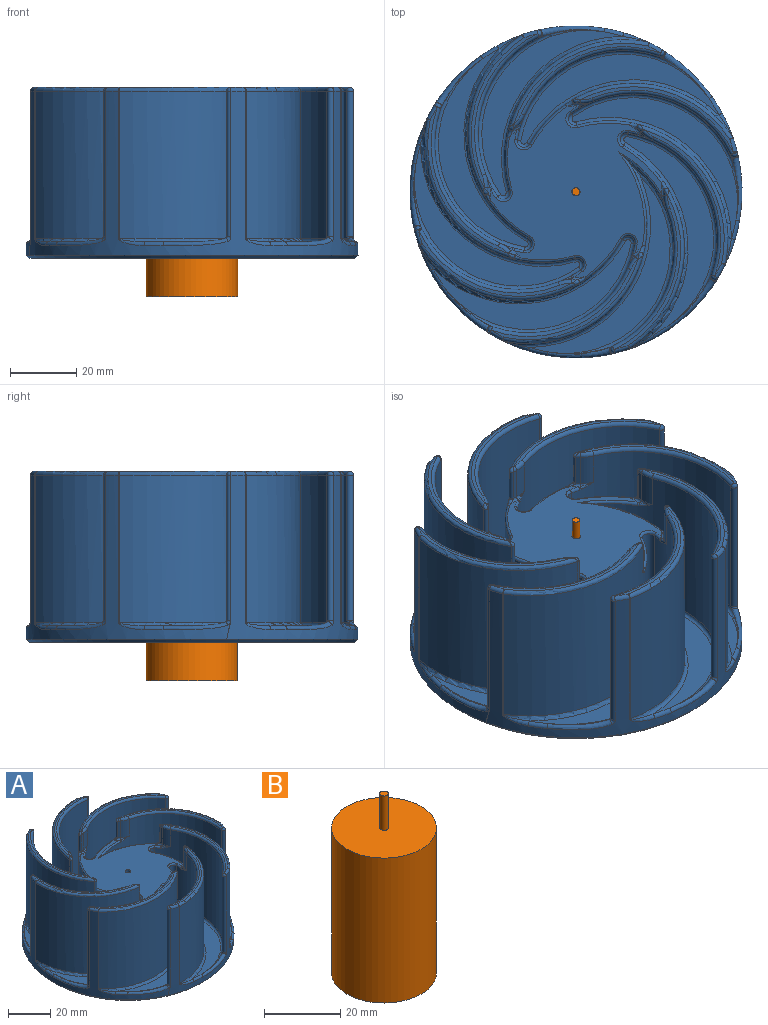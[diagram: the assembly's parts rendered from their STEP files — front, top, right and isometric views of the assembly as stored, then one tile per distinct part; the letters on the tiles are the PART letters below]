
ASSEMBLY  parts=2 mates=1
PART A: 279 faces, bbox 106.1x106.1x52.1 mm
  f0: bspline ~1.41x1mm, area 1.2mm2, adj f37,f60,f254,f256,f259
  f1: bspline ~1.5x1.09mm, area 1.2mm2, adj f31,f61,f234,f236,f239
  f2: bspline ~1.41x1mm, area 1.2mm2, adj f42,f62,f216,f218,f221
  f3: bspline ~1.5x1.09mm, area 1.2mm2, adj f39,f63,f196,f198,f201
  f4: bspline ~1.41x1mm, area 1.2mm2, adj f45,f64,f210,f211,f214
  f5: bspline ~1.5x1.09mm, area 1.2mm2, adj f44,f65,f231,f232,f235
  f6: bspline ~1.41x1mm, area 1.2mm2, adj f36,f66,f251,f252,f255
  f7: bspline ~1.5x1.09mm, area 1.2mm2, adj f33,f67,f269,f271,f272
  f8: bspline ~2.35x1.6mm, area 2.9mm2, adj f16,f32,f48,f153,f157
  f9: bspline ~2.3x1.86mm, area 2.9mm2, adj f17,f41,f48,f125,f126
  f10: bspline ~2.35x1.6mm, area 2.9mm2, adj f18,f40,f48,f97,f98
  f11: bspline ~2.3x1.86mm, area 2.9mm2, adj f19,f46,f48,f95,f99
  f12: bspline ~2.35x1.6mm, area 2.9mm2, adj f20,f43,f48,f123,f127
  f13: bspline ~2.3x1.86mm, area 2.9mm2, adj f21,f35,f48,f151,f154
  f14: bspline ~2.35x1.6mm, area 2.9mm2, adj f22,f34,f48,f178,f182
  f15: bspline ~2.3x1.86mm, area 2.9mm2, adj f23,f38,f48,f180,f181
  f16: bspline ~18.89x13.53mm, area 40.2mm2, adj f8,f48,f157,f161
  f17: bspline ~21.98x6.12mm, area 40.2mm2, adj f9,f48,f125,f134
  f18: bspline ~18.89x13.53mm, area 40.2mm2, adj f10,f48,f97,f106
  f19: bspline ~21.98x6.12mm, area 40.2mm2, adj f11,f48,f94,f95
  f20: bspline ~18.89x13.53mm, area 40.2mm2, adj f12,f48,f122,f123
  f21: bspline ~21.98x6.12mm, area 40.2mm2, adj f13,f48,f150,f151
  f22: bspline ~18.89x13.53mm, area 40.2mm2, adj f14,f48,f177,f178
  f23: bspline ~21.98x6.12mm, area 40.2mm2, adj f15,f48,f180,f189
  f24: plane 39.79x30.16mm, normal (0,0,1), area 51.4mm2, adj f183,f184,f187,f190,f191
  f25: plane 48.44x15.03mm, normal (0,0,1), area 51.4mm2, adj f166,f167,f171,f175,f176
  f26: plane 39.79x30.16mm, normal (0,0,1), area 51.4mm2, adj f139,f140,f144,f148,f149
  f27: plane 48.44x15.03mm, normal (0,0,1), area 51.4mm2, adj f111,f112,f116,f120,f121
  f28: plane 39.79x30.16mm, normal (0,0,1), area 51.4mm2, adj f84,f85,f88,f92,f93
  f29: plane 48.44x15.03mm, normal (0,0,1), area 51.4mm2, adj f100,f101,f104,f107,f108
  f30: plane 39.79x30.16mm, normal (0,0,1), area 51.4mm2, adj f128,f129,f132,f135,f136
  f31: cylinder r=35.7mm len=61.85mm, axis (0,0,1), area 3395.5mm2, adj f1,f32,f160,f167,f168,f233,f234,f236
  f32: cylinder r=32.5mm len=44.3mm, axis (0,0,1), area 2790.1mm2, adj f8,f31,f71,f148,f153,f157,f222,f225
  f33: cylinder r=35.7mm len=59.91mm, axis (0,0,1), area 3043.9mm2, adj f7,f78,f163,f169,f170,f270,f271,f272
  f34: cylinder r=32.5mm len=44.3mm, axis (0,0,1), area 2416.6mm2, adj f14,f69,f78,f178,f182,f183,f260,f262
  f35: cylinder r=32.5mm len=49.43mm, axis (0,0,1), area 2416.6mm2, adj f13,f76,f79,f151,f154,f155,f263,f264
  f36: cylinder r=35.7mm len=51.3mm, axis (0,0,1), area 3043.9mm2, adj f6,f79,f136,f142,f143,f251,f255,f258
  f37: cylinder r=35.7mm len=51.3mm, axis (0,0,1), area 3043.9mm2, adj f0,f77,f188,f191,f194,f253,f254,f256
  f38: cylinder r=32.5mm len=49.43mm, axis (0,0,1), area 2416.6mm2, adj f15,f70,f77,f175,f180,f181,f240,f242
  f39: cylinder r=35.7mm len=59.91mm, axis (0,0,1), area 3043.9mm2, adj f3,f82,f105,f112,f113,f196,f197,f198
  f40: cylinder r=32.5mm len=44.3mm, axis (0,0,1), area 2416.6mm2, adj f10,f73,f82,f92,f97,f98,f203,f204
  f41: cylinder r=32.5mm len=49.43mm, axis (0,0,1), area 2416.6mm2, adj f9,f72,f83,f120,f125,f126,f202,f205
  f42: cylinder r=35.7mm len=51.3mm, axis (0,0,1), area 3043.9mm2, adj f2,f83,f133,f140,f141,f215,f216,f218
  f43: cylinder r=32.5mm len=44.3mm, axis (0,0,1), area 2416.6mm2, adj f12,f75,f80,f123,f127,f128,f243,f244
  f44: cylinder r=35.7mm len=59.91mm, axis (0,0,1), area 3043.9mm2, adj f5,f80,f108,f114,f115,f231,f235,f238
  f45: cylinder r=35.7mm len=51.3mm, axis (0,0,1), area 3043.9mm2, adj f4,f81,f85,f86,f87,f210,f214,f217
  f46: cylinder r=32.5mm len=49.43mm, axis (0,0,1), area 2416.6mm2, adj f11,f74,f81,f95,f99,f100,f223,f224
  f47: plane 48.44x15.03mm, normal (0,0,1), area 51.4mm2, adj f155,f156,f159,f162,f163
  f48: cylinder r=50mm len=100mm, axis (0,0,-1), area 2743.9mm2, adj f8,f9,f10,f11,f12,f13,f14,f15
  f49: plane 98x98mm, normal (0,0,-1), area 6738.7mm2, adj f275,f276
  f50: cylinder r=15mm len=33mm, axis (0,0,-1), area 3110.2mm2, adj f275,f278
  f51: plane 28x28mm, normal (0,0,-1), area 599.8mm2, adj f277,f278
  f52: plane 57.4x36.6mm, normal (0,0,1), area 406mm2, adj f157,f160,f161
  f53: plane 57.4x32.34mm, normal (0,0,1), area 402.5mm2, adj f170,f174,f177,f178
  f54: plane 53.9x37.11mm, normal (0,0,1), area 402.5mm2, adj f143,f147,f150,f151
  f55: plane 53.9x37.11mm, normal (0,0,1), area 402.5mm2, adj f180,f185,f188,f189
  f56: plane 57.4x32.34mm, normal (0,0,1), area 402.5mm2, adj f97,f102,f105,f106
  f57: plane 53.9x37.11mm, normal (0,0,1), area 402.5mm2, adj f125,f130,f133,f134
  f58: plane 57.4x32.34mm, normal (0,0,1), area 402.5mm2, adj f115,f119,f122,f123
  f59: plane 53.9x37.11mm, normal (0,0,1), area 402.5mm2, adj f87,f91,f94,f95
  f60: cylinder r=26.54mm len=9.65mm, axis (0,0,1), area 12.9mm2, adj f0,f69,f187,f254,f259
  f61: cylinder r=26.54mm len=9.65mm, axis (0,0,1), area 12.9mm2, adj f1,f70,f166,f234,f239
  f62: cylinder r=26.54mm len=9.65mm, axis (0,0,1), area 12.9mm2, adj f2,f71,f139,f216,f221
  f63: cylinder r=26.54mm len=9.65mm, axis (0,0,1), area 12.9mm2, adj f3,f72,f111,f196,f201
  f64: cylinder r=26.54mm len=9.65mm, axis (0,0,1), area 12.9mm2, adj f4,f73,f84,f210,f211
  f65: cylinder r=26.54mm len=9.65mm, axis (0,0,1), area 12.9mm2, adj f5,f74,f104,f231,f232
  f66: cylinder r=26.54mm len=9.65mm, axis (0,0,1), area 12.9mm2, adj f6,f75,f132,f251,f252
  f67: cylinder r=26.54mm len=9.65mm, axis (0,0,1), area 12.9mm2, adj f7,f76,f159,f269,f272
  f68: plane 51.02x51.02mm, normal (0,0,1), area 1459.3mm2, adj f197,f200,f201,f204,f209,f211,f212,f215
  f69: cylinder r=10mm len=9.65mm, axis (0,0,1), area 40.6mm2, adj f34,f60,f184,f257
  f70: cylinder r=10mm len=9.65mm, axis (0,0,1), area 40.6mm2, adj f38,f61,f171,f237
  f71: cylinder r=10mm len=9.65mm, axis (0,0,1), area 40.6mm2, adj f32,f62,f144,f219
  f72: cylinder r=10mm len=9.65mm, axis (0,0,1), area 40.6mm2, adj f41,f63,f116,f199
  f73: cylinder r=10mm len=9.65mm, axis (0,0,1), area 40.6mm2, adj f40,f64,f88,f207
  f74: cylinder r=10mm len=9.65mm, axis (0,0,1), area 40.6mm2, adj f46,f65,f101,f227
  f75: cylinder r=10mm len=9.65mm, axis (0,0,1), area 40.6mm2, adj f43,f66,f129,f247
  f76: cylinder r=10mm len=9.65mm, axis (0,0,1), area 40.6mm2, adj f35,f67,f156,f266
  f77: cylinder r=2mm len=33.15mm, axis (0,0,1), area 186.1mm2, adj f37,f38,f185,f249
  f78: cylinder r=2mm len=33.15mm, axis (0,0,1), area 186.1mm2, adj f33,f34,f174,f268
  f79: cylinder r=2mm len=33.15mm, axis (0,0,1), area 186.1mm2, adj f35,f36,f147,f261
  f80: cylinder r=2mm len=33.15mm, axis (0,0,1), area 186.1mm2, adj f43,f44,f119,f241
  f81: cylinder r=2mm len=33.15mm, axis (0,0,1), area 186.1mm2, adj f45,f46,f91,f220
  f82: cylinder r=2mm len=33.15mm, axis (0,0,1), area 186.1mm2, adj f39,f40,f102,f200
  f83: cylinder r=2mm len=33.15mm, axis (0,0,1), area 186.1mm2, adj f41,f42,f130,f212
  f84: torus R=27.64mm, axis (0,0,1), area 1.5mm2, adj f28,f64,f88,f206
  f85: torus R=34.6mm, axis (0,0,1), area 91.4mm2, adj f28,f45,f89,f206
  f86: cylinder r=1.1mm len=44.3mm, axis (0,0,1), area 12mm2, adj f45,f48,f89,f90
  f87: torus R=36.8mm, axis (0,0,1), area 121.6mm2, adj f45,f59,f90,f91
  f88: torus R=8.9mm, axis (0,0,1), area 7mm2, adj f28,f73,f84,f92
  f89: sphere r=1.1mm, area 0.3mm2, adj f85,f86,f93
  f90: bspline ~9.7x2.31mm, area 9.2mm2, adj f48,f86,f87,f94
  f91: torus R=0.9mm, axis (0,0,1), area 7.8mm2, adj f59,f81,f87,f95
  f92: torus R=33.6mm, axis (0,0,1), area 85.2mm2, adj f28,f40,f88,f96
  f93: torus R=48.9mm, axis (0,0,1), area 7.7mm2, adj f28,f48,f89,f96
  f94: torus R=48.9mm, axis (0,0,1), area 10mm2, adj f19,f48,f59,f90
  f95: torus R=31.4mm, axis (0,0,1), area 109.6mm2, adj f11,f19,f46,f59,f91
  f96: sphere r=1.1mm, area 4.4mm2, adj f92,f93,f98
  f97: torus R=31.4mm, axis (0,0,1), area 109.6mm2, adj f10,f18,f40,f56,f102
  f98: cylinder r=1.1mm len=43.79mm, axis (0,0,-1), area 141.2mm2, adj f10,f40,f48,f96
  f99: cylinder r=1.1mm len=43.79mm, axis (0,0,-1), area 141.2mm2, adj f11,f46,f48,f103
  f100: torus R=33.6mm, axis (0,0,1), area 85.2mm2, adj f29,f46,f101,f103
  f101: torus R=8.9mm, axis (0,0,1), area 7mm2, adj f29,f74,f100,f104
  f102: torus R=0.9mm, axis (0,0,1), area 7.8mm2, adj f56,f82,f97,f105
  f103: sphere r=1.1mm, area 2.9mm2, adj f99,f100,f107
  f104: torus R=27.64mm, axis (0,0,1), area 1.5mm2, adj f29,f65,f101,f226
  f105: torus R=36.8mm, axis (0,0,1), area 121.6mm2, adj f39,f56,f102,f109
  f106: torus R=48.9mm, axis (0,0,1), area 10mm2, adj f18,f48,f56,f109
  f107: torus R=48.9mm, axis (0,0,1), area 7.7mm2, adj f29,f48,f103,f110
  f108: torus R=34.6mm, axis (0,0,1), area 91.4mm2, adj f29,f44,f110,f226
  f109: bspline ~8.1x6.51mm, area 9.2mm2, adj f48,f105,f106,f113
  f110: sphere r=1.1mm, area 0.3mm2, adj f107,f108,f114
  f111: torus R=27.64mm, axis (0,0,1), area 1.5mm2, adj f27,f63,f116,f195
  f112: torus R=34.6mm, axis (0,0,1), area 91.4mm2, adj f27,f39,f117,f195
  f113: cylinder r=1.1mm len=44.3mm, axis (0,0,1), area 12mm2, adj f39,f48,f109,f117
  f114: cylinder r=1.1mm len=44.3mm, axis (0,0,1), area 12mm2, adj f44,f48,f110,f118
  f115: torus R=36.8mm, axis (0,0,1), area 121.6mm2, adj f44,f58,f118,f119
  f116: torus R=8.9mm, axis (0,0,1), area 7mm2, adj f27,f72,f111,f120
  f117: sphere r=1.1mm, area 0.3mm2, adj f112,f113,f121
  f118: bspline ~8.1x6.51mm, area 9.2mm2, adj f48,f114,f115,f122
  f119: torus R=0.9mm, axis (0,0,1), area 7.8mm2, adj f58,f80,f115,f123
  f120: torus R=33.6mm, axis (0,0,1), area 85.2mm2, adj f27,f41,f116,f124
  f121: torus R=48.9mm, axis (0,0,1), area 7.7mm2, adj f27,f48,f117,f124
  f122: torus R=48.9mm, axis (0,0,1), area 10mm2, adj f20,f48,f58,f118
  f123: torus R=31.4mm, axis (0,0,1), area 109.6mm2, adj f12,f20,f43,f58,f119
  f124: sphere r=1.1mm, area 3.5mm2, adj f120,f121,f126
  f125: torus R=31.4mm, axis (0,0,1), area 109.6mm2, adj f9,f17,f41,f57,f130
  f126: cylinder r=1.1mm len=43.79mm, axis (0,0,-1), area 141.2mm2, adj f9,f41,f48,f124
  f127: cylinder r=1.1mm len=43.79mm, axis (0,0,-1), area 141.2mm2, adj f12,f43,f48,f131
  f128: torus R=33.6mm, axis (0,0,1), area 85.2mm2, adj f30,f43,f129,f131
  f129: torus R=8.9mm, axis (0,0,1), area 7mm2, adj f30,f75,f128,f132
  f130: torus R=0.9mm, axis (0,0,1), area 7.8mm2, adj f57,f83,f125,f133
  f131: sphere r=1.1mm, area 2.9mm2, adj f127,f128,f135
  f132: torus R=27.64mm, axis (0,0,1), area 1.5mm2, adj f30,f66,f129,f246
  f133: torus R=36.8mm, axis (0,0,1), area 121.6mm2, adj f42,f57,f130,f137
  f134: torus R=48.9mm, axis (0,0,1), area 10mm2, adj f17,f48,f57,f137
  f135: torus R=48.9mm, axis (0,0,1), area 7.7mm2, adj f30,f48,f131,f138
  f136: torus R=34.6mm, axis (0,0,1), area 91.4mm2, adj f30,f36,f138,f246
  f137: bspline ~9.7x2.31mm, area 9.2mm2, adj f48,f133,f134,f141
  f138: sphere r=1.1mm, area 0.3mm2, adj f135,f136,f142
  f139: torus R=27.64mm, axis (0,0,1), area 1.5mm2, adj f26,f62,f144,f213
  f140: torus R=34.6mm, axis (0,0,1), area 91.4mm2, adj f26,f42,f145,f213
  f141: cylinder r=1.1mm len=44.3mm, axis (0,0,1), area 12mm2, adj f42,f48,f137,f145
  f142: cylinder r=1.1mm len=44.3mm, axis (0,0,1), area 12mm2, adj f36,f48,f138,f146
  f143: torus R=36.8mm, axis (0,0,1), area 121.6mm2, adj f36,f54,f146,f147
  f144: torus R=8.9mm, axis (0,0,1), area 7mm2, adj f26,f71,f139,f148
  f145: sphere r=1.1mm, area 0.3mm2, adj f140,f141,f149
  f146: bspline ~9.7x2.31mm, area 9.2mm2, adj f48,f142,f143,f150
  f147: torus R=0.9mm, axis (0,0,1), area 7.8mm2, adj f54,f79,f143,f151
  f148: torus R=33.6mm, axis (0,0,1), area 85.2mm2, adj f26,f32,f144,f152
  f149: torus R=48.9mm, axis (0,0,1), area 7.7mm2, adj f26,f48,f145,f152
  f150: torus R=48.9mm, axis (0,0,1), area 10mm2, adj f21,f48,f54,f146
  f151: torus R=31.4mm, axis (0,0,1), area 109.6mm2, adj f13,f21,f35,f54,f147
  f152: sphere r=1.1mm, area 3.5mm2, adj f148,f149,f153
  f153: cylinder r=1.1mm len=43.79mm, axis (0,0,-1), area 141.2mm2, adj f8,f32,f48,f152
  f154: cylinder r=1.1mm len=43.79mm, axis (0,0,-1), area 141.2mm2, adj f13,f35,f48,f158
  f155: torus R=33.6mm, axis (0,0,1), area 85.2mm2, adj f35,f47,f156,f158
  f156: torus R=8.9mm, axis (0,0,1), area 7mm2, adj f47,f76,f155,f159
  f157: torus R=31.4mm, axis (0,0,1), area 123.9mm2, adj f8,f16,f32,f52,f160
  f158: sphere r=1.1mm, area 3.1mm2, adj f154,f155,f162
  f159: torus R=27.64mm, axis (0,0,1), area 1.5mm2, adj f47,f67,f156,f273
  f160: torus R=36.8mm, axis (0,0,1), area 135.1mm2, adj f31,f52,f157,f164
  f161: torus R=48.9mm, axis (0,0,1), area 10mm2, adj f16,f48,f52,f164
  f162: torus R=48.9mm, axis (0,0,1), area 7.7mm2, adj f47,f48,f158,f165
  f163: torus R=34.6mm, axis (0,0,1), area 91.4mm2, adj f33,f47,f165,f273
  f164: bspline ~8.1x6.51mm, area 9.2mm2, adj f48,f160,f161,f168
  f165: sphere r=1.1mm, area 0.3mm2, adj f162,f163,f169
  f166: torus R=27.64mm, axis (0,0,1), area 1.5mm2, adj f25,f61,f171,f230
  f167: torus R=34.6mm, axis (0,0,1), area 91.4mm2, adj f25,f31,f172,f230
  f168: cylinder r=1.1mm len=44.3mm, axis (0,0,1), area 12mm2, adj f31,f48,f164,f172
  f169: cylinder r=1.1mm len=44.3mm, axis (0,0,1), area 12mm2, adj f33,f48,f165,f173
  f170: torus R=36.8mm, axis (0,0,1), area 121.6mm2, adj f33,f53,f173,f174
  f171: torus R=8.9mm, axis (0,0,1), area 7mm2, adj f25,f70,f166,f175
  f172: sphere r=1.1mm, area 0.3mm2, adj f167,f168,f176
  f173: bspline ~8.1x6.51mm, area 9.2mm2, adj f48,f169,f170,f177
  f174: torus R=0.9mm, axis (0,0,1), area 7.8mm2, adj f53,f78,f170,f178
  f175: torus R=33.6mm, axis (0,0,1), area 85.2mm2, adj f25,f38,f171,f179
  f176: torus R=48.9mm, axis (0,0,1), area 7.7mm2, adj f25,f48,f172,f179
  f177: torus R=48.9mm, axis (0,0,1), area 10mm2, adj f22,f48,f53,f173
  f178: torus R=31.4mm, axis (0,0,1), area 109.6mm2, adj f14,f22,f34,f53,f174
  f179: sphere r=1.1mm, area 2.9mm2, adj f175,f176,f181
  f180: torus R=31.4mm, axis (0,0,1), area 109.6mm2, adj f15,f23,f38,f55,f185
  f181: cylinder r=1.1mm len=43.79mm, axis (0,0,-1), area 141.2mm2, adj f15,f38,f48,f179
  f182: cylinder r=1.1mm len=43.79mm, axis (0,0,-1), area 141.2mm2, adj f14,f34,f48,f186
  f183: torus R=33.6mm, axis (0,0,1), area 85.2mm2, adj f24,f34,f184,f186
  f184: torus R=8.9mm, axis (0,0,1), area 7mm2, adj f24,f69,f183,f187
  f185: torus R=0.9mm, axis (0,0,1), area 7.8mm2, adj f55,f77,f180,f188
  f186: sphere r=1.1mm, area 3.6mm2, adj f182,f183,f190
  f187: torus R=27.64mm, axis (0,0,1), area 1.5mm2, adj f24,f60,f184,f250
  f188: torus R=36.8mm, axis (0,0,1), area 121.6mm2, adj f37,f55,f185,f192
  f189: torus R=48.9mm, axis (0,0,1), area 10mm2, adj f23,f48,f55,f192
  f190: torus R=48.9mm, axis (0,0,1), area 7.7mm2, adj f24,f48,f186,f193
  f191: torus R=34.6mm, axis (0,0,1), area 91.4mm2, adj f24,f37,f193,f250
  f192: bspline ~9.7x2.31mm, area 9.2mm2, adj f48,f188,f189,f194
  f193: sphere r=1.1mm, area 0.3mm2, adj f190,f191,f194
  f194: cylinder r=1.1mm len=44.3mm, axis (0,0,1), area 12mm2, adj f37,f48,f192,f193
  f195: bspline ~3.91x2.13mm, area 2.3mm2, adj f111,f112,f196
  f196: cylinder r=0.75mm len=9.49mm, axis (0,0,-1), area 18.7mm2, adj f3,f39,f63,f195
  f197: torus R=34.95mm, axis (0,0,1), area 19mm2, adj f39,f68,f198,f200
  f198: bspline ~2.87x2.55mm, area 3.6mm2, adj f3,f39,f197,f201
  f199: torus R=10.75mm, axis (0,0,1), area 2.2mm2, adj f72,f201,f202
  f200: torus R=2.75mm, axis (0,0,1), area 7.5mm2, adj f68,f82,f197,f204
  f201: torus R=25.79mm, axis (0,0,1), area 2.7mm2, adj f3,f63,f68,f198,f199,f205
  f202: bspline ~4.36x2.79mm, area 1.5mm2, adj f41,f199,f205
  f203: bspline ~4.71x1.53mm, area 1.5mm2, adj f40,f207,f208
  f204: torus R=33.25mm, axis (0,0,1), area 3.5mm2, adj f40,f68,f200,f208
  f205: bspline ~1.55x1.22mm, area 0.6mm2, adj f41,f201,f202,f209
  f206: bspline ~4.04x2.13mm, area 2.3mm2, adj f84,f85,f210
  f207: torus R=10.75mm, axis (0,0,1), area 2.2mm2, adj f73,f203,f211
  f208: bspline ~1.34x0.98mm, area 0.6mm2, adj f40,f203,f204,f211
  f209: torus R=33.25mm, axis (0,0,1), area 3.5mm2, adj f41,f68,f205,f212
  f210: cylinder r=0.75mm len=9.49mm, axis (0,0,-1), area 18.7mm2, adj f4,f45,f64,f206
  f211: torus R=25.79mm, axis (0,0,1), area 2.7mm2, adj f4,f64,f68,f207,f208,f214
  f212: torus R=2.75mm, axis (0,0,1), area 7.5mm2, adj f68,f83,f209,f215
  f213: bspline ~4.04x2.13mm, area 2.3mm2, adj f139,f140,f216
  f214: bspline ~3.08x2.28mm, area 3.6mm2, adj f4,f45,f211,f217
  f215: torus R=34.95mm, axis (0,0,1), area 19mm2, adj f42,f68,f212,f218
  f216: cylinder r=0.75mm len=9.49mm, axis (0,0,-1), area 18.7mm2, adj f2,f42,f62,f213
  f217: torus R=34.95mm, axis (0,0,1), area 19mm2, adj f45,f68,f214,f220
  f218: bspline ~3.08x2.28mm, area 3.6mm2, adj f2,f42,f215,f221
  f219: torus R=10.75mm, axis (0,0,1), area 2.2mm2, adj f71,f221,f222
  f220: torus R=2.75mm, axis (0,0,1), area 7.5mm2, adj f68,f81,f217,f224
  f221: torus R=25.79mm, axis (0,0,1), area 2.7mm2, adj f2,f62,f68,f218,f219,f225
  f222: bspline ~4.71x1.53mm, area 1.5mm2, adj f32,f219,f225
  f223: bspline ~4.36x2.79mm, area 1.5mm2, adj f46,f227,f228
  f224: torus R=33.25mm, axis (0,0,1), area 3.5mm2, adj f46,f68,f220,f228
  f225: bspline ~1.15x0.96mm, area 0.6mm2, adj f32,f221,f222,f229
  f226: bspline ~3.91x2.13mm, area 2.3mm2, adj f104,f108,f231
  f227: torus R=10.75mm, axis (0,0,1), area 2.2mm2, adj f74,f223,f232
  f228: bspline ~1.55x1.22mm, area 0.6mm2, adj f46,f223,f224,f232
  f229: torus R=33.25mm, axis (0,0,1), area 19.1mm2, adj f32,f68,f225,f233
  f230: bspline ~3.91x2.13mm, area 2.3mm2, adj f166,f167,f234
  f231: cylinder r=0.75mm len=9.49mm, axis (0,0,-1), area 18.7mm2, adj f5,f44,f65,f226
  f232: torus R=25.79mm, axis (0,0,1), area 2.7mm2, adj f5,f65,f68,f227,f228,f235
  f233: torus R=34.95mm, axis (0,0,1), area 33.6mm2, adj f31,f68,f229,f236
  f234: cylinder r=0.75mm len=9.49mm, axis (0,0,-1), area 18.7mm2, adj f1,f31,f61,f230
  f235: bspline ~2.87x2.55mm, area 3.6mm2, adj f5,f44,f232,f238
  f236: bspline ~2.87x2.55mm, area 3.6mm2, adj f1,f31,f233,f239
  f237: torus R=10.75mm, axis (0,0,1), area 2.2mm2, adj f70,f239,f240
  f238: torus R=34.95mm, axis (0,0,1), area 19mm2, adj f44,f68,f235,f241
  f239: torus R=25.79mm, axis (0,0,1), area 2.7mm2, adj f1,f61,f68,f236,f237,f242
  f240: bspline ~4.36x2.79mm, area 1.5mm2, adj f38,f237,f242
  f241: torus R=2.75mm, axis (0,0,1), area 7.5mm2, adj f68,f80,f238,f244
  f242: bspline ~1.55x1.22mm, area 0.6mm2, adj f38,f239,f240,f245
  f243: bspline ~4.71x1.53mm, area 1.5mm2, adj f43,f247,f248
  f244: torus R=33.25mm, axis (0,0,1), area 3.5mm2, adj f43,f68,f241,f248
  f245: torus R=33.25mm, axis (0,0,1), area 3.5mm2, adj f38,f68,f242,f249
  f246: bspline ~4.04x2.13mm, area 2.3mm2, adj f132,f136,f251
  f247: torus R=10.75mm, axis (0,0,1), area 2.2mm2, adj f75,f243,f252
  f248: bspline ~1.34x0.98mm, area 0.6mm2, adj f43,f243,f244,f252
  f249: torus R=2.75mm, axis (0,0,1), area 7.5mm2, adj f68,f77,f245,f253
  f250: bspline ~4.04x2.13mm, area 2.3mm2, adj f187,f191,f254
  f251: cylinder r=0.75mm len=9.49mm, axis (0,0,-1), area 18.7mm2, adj f6,f36,f66,f246
  f252: torus R=25.79mm, axis (0,0,1), area 2.7mm2, adj f6,f66,f68,f247,f248,f255
  f253: torus R=34.95mm, axis (0,0,1), area 19mm2, adj f37,f68,f249,f256
  f254: cylinder r=0.75mm len=9.49mm, axis (0,0,-1), area 18.7mm2, adj f0,f37,f60,f250
  f255: bspline ~3.08x2.28mm, area 3.6mm2, adj f6,f36,f252,f258
  f256: bspline ~3.08x2.28mm, area 3.6mm2, adj f0,f37,f253,f259
  f257: torus R=10.75mm, axis (0,0,1), area 2.2mm2, adj f69,f259,f260
  f258: torus R=34.95mm, axis (0,0,1), area 19mm2, adj f36,f68,f255,f261
  f259: torus R=25.79mm, axis (0,0,1), area 2.7mm2, adj f0,f60,f68,f256,f257,f262
  f260: bspline ~4.71x1.53mm, area 1.5mm2, adj f34,f257,f262
  f261: torus R=2.75mm, axis (0,0,1), area 7.5mm2, adj f68,f79,f258,f264
  f262: bspline ~1.15x0.96mm, area 0.6mm2, adj f34,f259,f260,f265
  f263: bspline ~4.36x2.79mm, area 1.5mm2, adj f35,f266,f267
  f264: torus R=33.25mm, axis (0,0,1), area 3.5mm2, adj f35,f68,f261,f267
  f265: torus R=33.25mm, axis (0,0,1), area 3.5mm2, adj f34,f68,f262,f268
  f266: torus R=10.75mm, axis (0,0,1), area 2.2mm2, adj f76,f263,f269
  f267: bspline ~1.55x1.22mm, area 0.6mm2, adj f35,f263,f264,f269
  f268: torus R=2.75mm, axis (0,0,1), area 7.5mm2, adj f68,f78,f265,f270
  f269: torus R=25.79mm, axis (0,0,1), area 2.7mm2, adj f7,f67,f68,f266,f267,f271
  f270: torus R=34.95mm, axis (0,0,1), area 19mm2, adj f33,f68,f268,f271
  f271: bspline ~2.87x2.55mm, area 3.6mm2, adj f7,f33,f269,f270
  f272: cylinder r=0.75mm len=9.49mm, axis (0,0,-1), area 18.7mm2, adj f7,f33,f67,f273
  f273: bspline ~3.91x2.13mm, area 2.3mm2, adj f159,f163,f272
  f274: cylinder r=1.25mm len=4mm, axis (0,0,-1), area 31.4mm2, adj f68,f277
  f275: cone r=16mm half-angle=45deg, axis (0,0,-1), area 137.7mm2, adj f49,f50
  f276: cone r=50mm half-angle=45deg, axis (0,0,1), area 439.8mm2, adj f48,f49
  f277: cone r=1.25mm half-angle=45deg, axis (0,0,-1), area 15.6mm2, adj f51,f274
  f278: cone r=15mm half-angle=45deg, axis (0,0,-1), area 128.8mm2, adj f50,f51
PART B: 5 faces, bbox 27.5x27.5x57.5 mm
  f0: cylinder r=13.75mm len=46.5mm, axis (0,0,-1), area 4017.3mm2, adj f1,f2
  f1: plane 27.5x27.5mm, normal (0,0,1), area 589.8mm2, adj f0,f3
  f2: plane 27.5x27.5mm, normal (0,0,-1), area 594mm2, adj f0
  f3: cylinder r=1.15mm len=11mm, axis (0,0,-1), area 79.5mm2, adj f1,f4
  f4: plane 2.3x2.3mm, normal (0,0,1), area 4.2mm2, adj f3
PLACE A rot(axis=(0,0,-1),55deg) t=(53.59,-5.29,30.32)mm
PLACE B t=(53.59,-5.29,42.07)mm fixed
MATE revolute B.f0 <-> A.f50  axis (0,0,1) through (53.59,-5.29,65.32)mm
